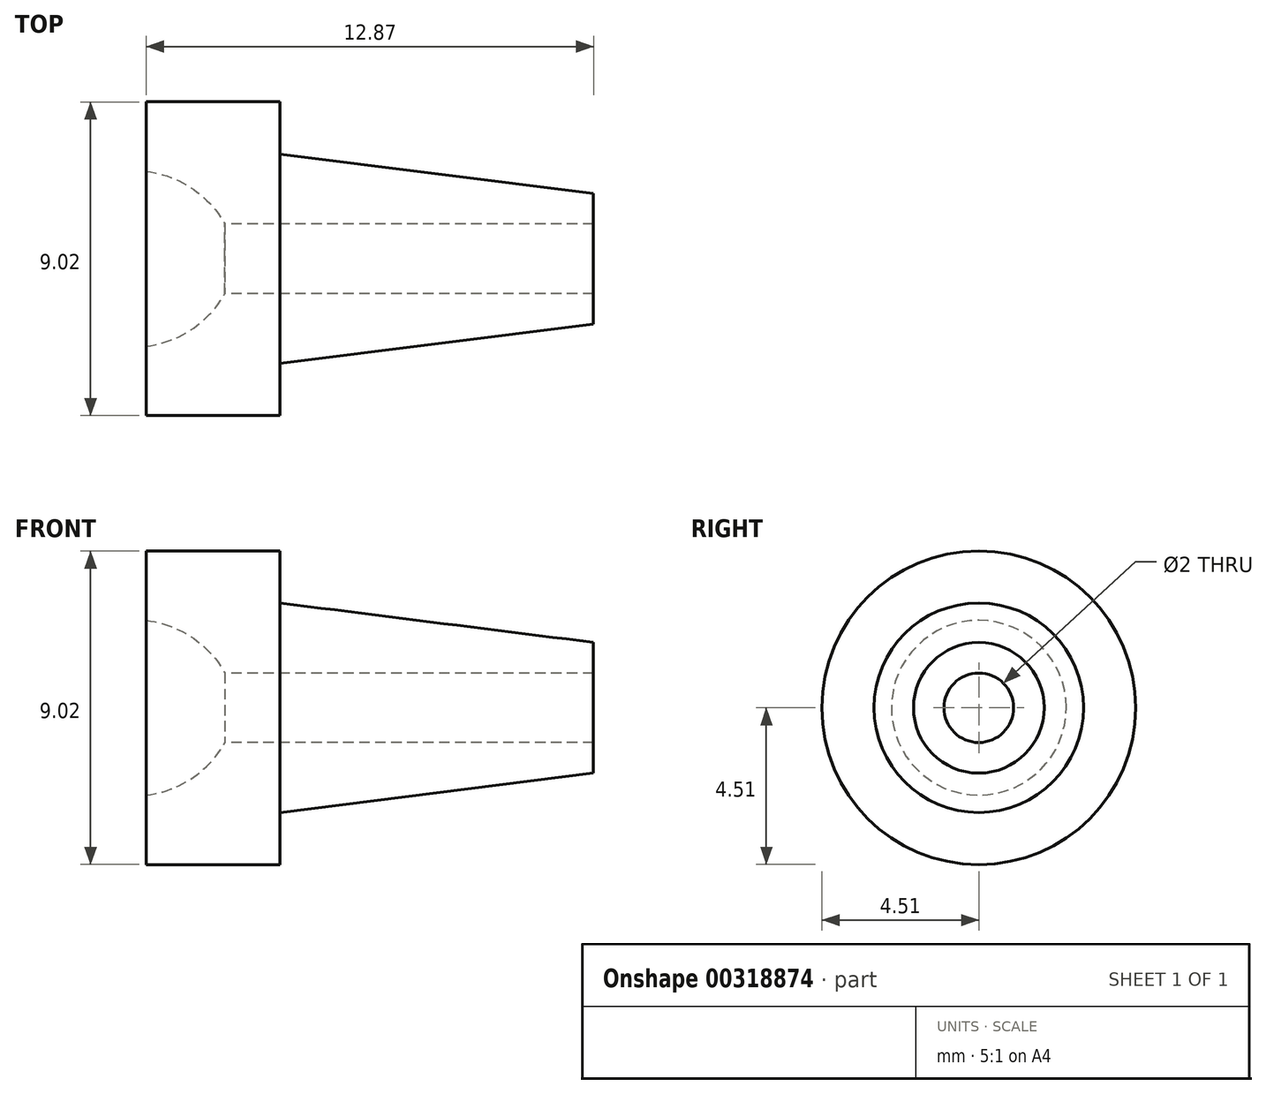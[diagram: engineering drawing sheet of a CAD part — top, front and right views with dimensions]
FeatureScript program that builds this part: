
annotation { "Feature Type Name" : "Feature", "Feature Type Description" : "" }
export const myFeature = defineFeature(function(context is Context, id is Id, definition is map)
    precondition{}
    {
        {
            var Q0;
            Q0=qCreatedBy(makeId("Top.planeOp"),FACE);
            var sketch = newSketch(context, id + "F0", { "sketchPlane" : qUnion([Q0])});
            skLineSegment(sketch, "E0", {"start": v(-14.71, 4.51) * mm, "end": v(-10.86, 4.51) * mm});
            skLineSegment(sketch, "E1", {"start": v(-10.86, 4.51) * mm, "end": v(-10.86, 3.01) * mm});
            skLineSegment(sketch, "E2", {"start": v(-10.86, 3.01) * mm, "end": v(-1.84, 1.88) * mm});
            skLineSegment(sketch, "E3", {"start": v(-32.24, 0) * mm, "end": v(-18.22, 0) * mm, "construction": true});
            skLineSegment(sketch, "E4", {"start": v(-12.45, 1) * mm, "end": v(-1.84, 1) * mm});
            skLineSegment(sketch, "E5", {"start": v(-14.71, 4.51) * mm, "end": v(-14.71, 2.51) * mm});
            skLineSegment(sketch, "E6", {"start": v(-1.84, 1.88) * mm, "end": v(-1.84, 1) * mm});
            skArc(sketch, "E7", {"start": v(-12.45, 1) * mm, "mid": v(-13.4, 2.03) * mm, "end": v(-14.71, 2.51) * mm});
            skSolve(sketch);
        }
        {
            var Q0;
            Q0=makeQuery(id+"F0.imprint","IMPRINT",FACE,{"disambiguationData":[TD([[makeQuery(id+"F0.imprint","IMPRINT",EDGE,{"derivedFrom":sQuery(id+"F0.wireOp",EDGE,"E0")}),-1.0]])]});
            var Q1;
            Q1=sQuery(id+"F0.wireOp",EDGE,"E3");
            revolve(context, id + "F1", {"entities" : qUnion([Q0]), "axis" : qUnion([Q1]), "revolveType" : RevolveType.FULL});
        }
    });
